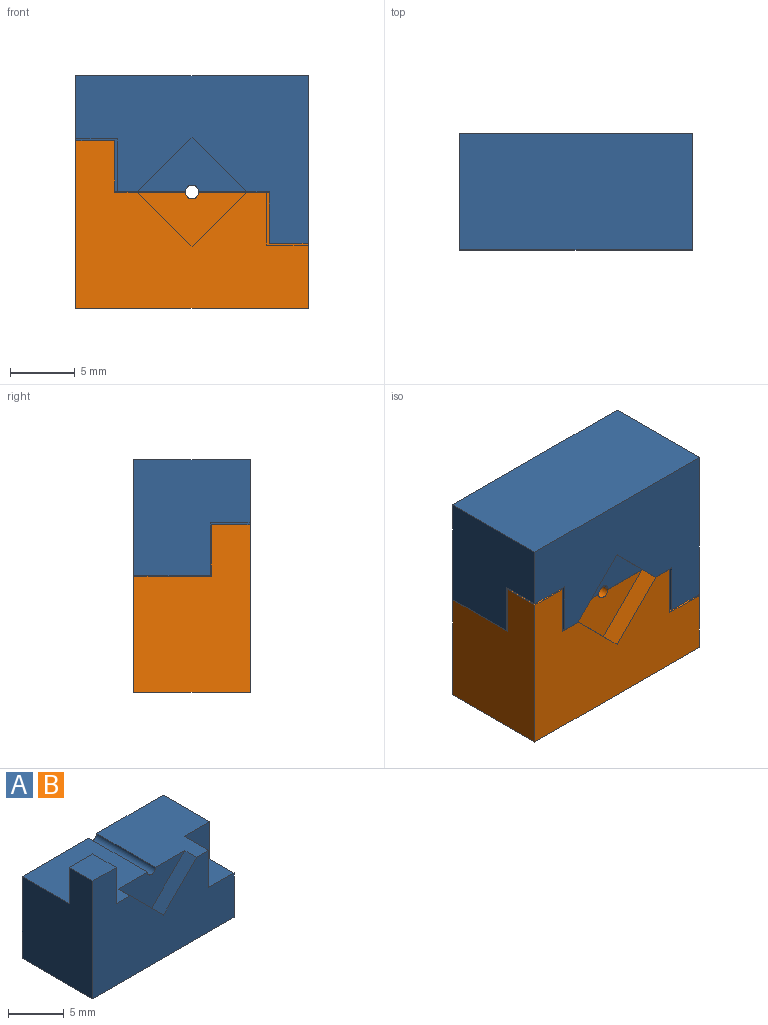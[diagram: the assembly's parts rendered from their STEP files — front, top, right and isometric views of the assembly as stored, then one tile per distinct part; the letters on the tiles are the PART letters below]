
ASSEMBLY  parts=2 mates=1
PART A: 17 faces, bbox 18x9x13 mm
  f0: plane 18x13mm, normal (0,-1,0), area 142.9mm2, adj f1,f2,f3,f4,f5,f7,f8,f12
  f1: plane 9x9mm, normal (1,0,0), area 68.3mm2, adj f0,f3,f5,f6,f14,f16
  f2: plane 9x8.49mm, normal (0,0,1), area 61.7mm2, adj f0,f4,f6,f8,f9,f10,f11,f12
  f3: plane 9x8.49mm, normal (0,0,1), area 60.9mm2, adj f0,f1,f6,f7,f9,f10,f14,f15
  f4: plane 13x9mm, normal (-1,0,0), area 93mm2, adj f0,f2,f5,f6,f11,f13
  f5: plane 18x9mm, normal (0,0,-1), area 162mm2, adj f0,f1,f4,f6
  f6: plane 18x9mm, normal (0,1,0), area 161.6mm2, adj f1,f2,f3,f4,f5,f10
  f7: plane 4.24x4.24mm, normal (-0.71,0,0.71), area 9mm2, adj f0,f3,f8,f9
  f8: plane 4.24x4.24mm, normal (0.71,0,0.71), area 9mm2, adj f0,f2,f7,f9
  f9: plane 8.49x4.24mm, normal (0,-1,0), area 17.6mm2, adj f2,f3,f7,f8,f10
  f10: cylinder r=0.52mm len=7.5mm, axis (0,-1,0), area 12.1mm2, adj f2,f3,f6,f9
  f11: plane 4x3mm, normal (0,1,0), area 12mm2, adj f2,f4,f12,f13
  f12: plane 4x3.01mm, normal (1,0,0), area 12mm2, adj f0,f2,f11,f13
  f13: plane 3.01x3mm, normal (0,0,1), area 9mm2, adj f0,f4,f11,f12
  f14: plane 4.1x3.2mm, normal (0,-1,0), area 13.1mm2, adj f1,f3,f15,f16
  f15: plane 4.1x3.1mm, normal (1,0,0), area 12.7mm2, adj f0,f3,f14,f16
  f16: plane 3.2x3.1mm, normal (0,0,1), area 9.9mm2, adj f0,f1,f14,f15
PART B: same geometry as A
PLACE A rot(axis=(0,1,0),180deg) t=(2.56,0.97,14.35)mm
PLACE B t=(-15.44,0.97,-3.67)mm fixed
MATE slider B.f3 <-> A.f2  axis (0,0,1) through (2.56,0.97,5.33)mm
